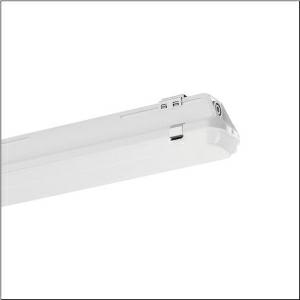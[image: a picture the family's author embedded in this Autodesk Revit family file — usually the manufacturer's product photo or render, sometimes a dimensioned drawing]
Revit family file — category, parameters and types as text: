
# Revit family: monsun_r__11_parking_51fg20dp440l_74b4
name_source: partatom
category: Lighting Fixtures
units: mm (PartAtom-declared; Revit-internal decimal feet)

## family parameters
Cut with Voids When Loaded = No
Host = Face
Light Source = No
Part Type = Normal
Room Calculation Point = No
Round Connector Dimension = Use Diameter
Shared = No

## types (1)
- --- (1 x LED, 4840 lm, 28.1 W, 4000K)
    Apparent Load = 28 VA
    CIE Flux Codes = 45 75 93 94 100
    Color Rendering = 80
    Color Temperature = 4000K
    Default Elevation = 1800 mm
    Description = Monsun® 11 parking, damp-proof luminaire, chain hanger, primary optical cover: enclosure, of PC, light emission: direct distribution, primary light characteristic: symmetric, installation type: suspended mounting, surface-mounted, horizontal mounting, vertical mounting, LED, rated luminous flux: 4.840lm, luminous efficacy: 172lm/W, light colour: 840, colour temperature: 4000K, control gear: DALI 2, with terminal, 5-pole, max. 2.5mm², mains connection: 220..240V, AC, 50/60Hz, rated input power: 28W, housing, of glass-fibre reinforced polyester, uncoated, bright grey, incl. chain hanger, length: 1.590mm, width: 90mm, height: 88mm, clip for enclosure, of stainless steel (V2A), ceiling mounting element, of stainless steel (V2A), chain hanger, of stainless steel (V2A), protection rating (complete): IP66, insulation class (complete): insulation class I (protective earthing), certification: CE, ENEC, VDE, UKCA, protection symbol: D, impact resistance: IK08, permissible operating ambient temperature: -25..+40°C, standard: EN 50419, EN 60598-2-1, corresponds to IFS (International Featured Standards) requirements for safety and quality in the food industry, for indoor or canopied outdoor use, no direct snow, no direct sun, no direct rain, LABS conformity tested according to VDMA 24364:2018-05, contact your sales advisor before using the luminaires in applications with unclear chemical exposure, large temperature fluctuations or condensation-forming humidity, packaging unit: 1 piece
    Height = 89 mm
    Lamp = 1 x LED
    Lamp Light Flux = 4840 lm
    Lamp Power = 28.1 W
    Lamp count = 1
    Length = 1590 mm
    Luminous efficacy = 172 lm/W
    Manufacturer = Siteco
    ModVariant = No
    Model = 51FG20DP440L
    Mounting Place = Ceiling
    Mounting Type = Surface mounted
    Number of Poles = 1
    OnlyDefault = Yes
    Power Factor = 1
    Product Name = Monsun® 11 parking
    Product group = damp-proof luminaire
    ProductGroupID = 301
    Protection Class = Protection class I
    Protection Degree = IP 66
    RLX_Detail_Level = 1
    RLX_Emergency_Light_Flux = 0 lm
    RLX_Emergency_Type = 0
    RLX_Emergency_Type_DB = No
    RlxData = <blob elided: 92321 chars, md5=eb9af930>
    Socket = socket
    Standby Power = 0 W
    System Light Flux = 4840 lm
    System Power = 28 W
    Type Comments = factory setting: luminous flux: 100 % | dim-lin: 254 | 193 mA
    Type Image = l_1349237.jpg
    URL = http://relux.com
    VarID = @adj_037619
    Voltage = 0 V
    Weight = 0.00 kg
    Width = 90 mm

## geometry (parser evidence)
native form markers: Blend x4, Sweep x13
no freeform markers — native parametric forms only
